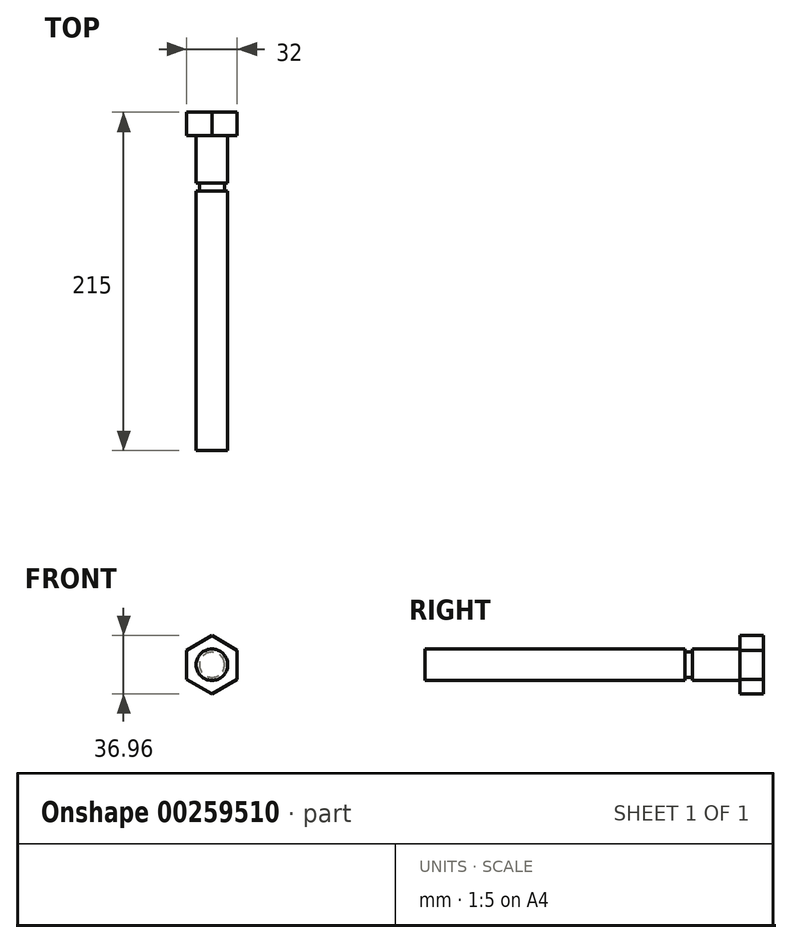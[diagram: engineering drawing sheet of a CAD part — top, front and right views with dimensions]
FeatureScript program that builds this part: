
annotation { "Feature Type Name" : "Feature", "Feature Type Description" : "" }
export const myFeature = defineFeature(function(context is Context, id is Id, definition is map)
    precondition{}
    {
        {
            var Q0;
            Q0=qCreatedBy(makeId("Front.planeOp"),FACE);
            var sketch = newSketch(context, id + "F0", { "sketchPlane" : qUnion([Q0])});
            skCircle(sketch, "E0", {"center": v(0, 0) * mm, "radius": 10 * mm});
            skSolve(sketch);
        }
        {
            var Q0;
            Q0 = qSketchRegion(id + "F0", true);
            extrude(context, id + "F1", {"entities" : qUnion([Q0]), "depth" : 200 * mm});
        }
        {
            var Q0;
            Q0=qCreatedBy(makeId("Front.planeOp"),FACE);
            cPlane(context, id + "F2", {"entities" : qUnion([Q0]), "cplaneType" : CPlaneType.OFFSET, "offset" : 30 * mm, "width" : 150 * mm, "height" : 150 * mm});
        }
        {
            var Q0;
            Q0=qCreatedBy(id+"F2.planeOp",FACE);
            var sketch = newSketch(context, id + "F3", { "sketchPlane" : qUnion([Q0])});
            skCircle(sketch, "E1", {"center": v(0, 0) * mm, "radius": 8 * mm});
            skCircle(sketch, "E2", {"center": v(0, 0) * mm, "radius": 10 * mm});
            skSolve(sketch);
        }
        {
            var Q0;
            Q0 = qSketchRegion(id + "F3", true);
            extrude(context, id + "F4", {"entities" : qUnion([Q0]), "operationType" : NewBodyOperationType.REMOVE, "depth" : 5 * mm});
        }
        {
            var Q0;
            Q0=makeQuery(id+"F1.opExtrude","CAP_FACE",FACE,{"disambiguationData":[OSD([sQuery(id+"F0.wireOp",EDGE,"E0")])],"isStart":true});
            var sketch = newSketch(context, id + "F5", { "sketchPlane" : qUnion([Q0])});
            skCircle(sketch, "E3.cCircle", {"center": v(0, 0) * mm, "radius": 16 * mm, "construction": true});
            skLineSegment(sketch, "E3.0", {"start": v(16, 9.24) * mm, "end": v(16, -9.24) * mm});
            skLineSegment(sketch, "E3.1", {"start": v(16, -9.24) * mm, "end": v(0, -18.48) * mm});
            skLineSegment(sketch, "E3.2", {"start": v(0, -18.48) * mm, "end": v(-16, -9.24) * mm});
            skLineSegment(sketch, "E3.3", {"start": v(-16, -9.24) * mm, "end": v(-16, 9.24) * mm});
            skLineSegment(sketch, "E3.4", {"start": v(-16, 9.24) * mm, "end": v(0, 18.48) * mm});
            skLineSegment(sketch, "E3.5", {"start": v(0, 18.48) * mm, "end": v(16, 9.24) * mm});
            skPoint(sketch, "E3.0.midPoint", {"position": v(16, 0) * mm});
            skSolve(sketch);
        }
        {
            var Q0;
            Q0 = qSketchRegion(id + "F5", true);
            extrude(context, id + "F6", {"entities" : qUnion([Q0]), "operationType" : NewBodyOperationType.ADD, "depth" : 15 * mm});
        }
    });
